# Revit family: L&L_LUCE&LIGHT_SIRI_BLVD_2.0
name_source: partatom
category: Lighting Fixtures
revit_build: Autodesk Revit 2018 (Build: 20181011_1500(x64)
units: mm (PartAtom-declared; Revit-internal decimal feet)

## family parameters
Cut with Voids When Loaded = No
Host = Face
Light Source = Yes
Part Type = Normal
Room Calculation Point = No
Round Connector Dimension = Use Diameter
Shared = No

## types (4) — shared parameters
BIM BADGE = https://bim.archiproducts.com
BODY MATERIAL = DIE-CAST ALUMINIUM ALLOY EN AB 47100
Color Filter = 16777215
Default Elevation = 1219 mm
Description = Urban lighting, projector on arm.
Dimming Lamp Color Temperature Shift = <None>
ENERGY EFFIECIENCY CLASS = A / A+ / A++
Emit Shape Visible in Rendering = Yes
Emit from Rectangle Length = 140 mm  [stored 0.459318 ft]
Emit from Rectangle Width = 120 mm  [stored 0.393701 ft]
HEIGHT = 124 mm  [stored 0.406824 ft]
ILLUMINITECHNICAL PERFORMANCE = 3000K - 38W - 230Vac
LENGTH = 680 mm  [stored 2.23097 ft]
Lamp = LED colour white: 2700K, 3000K, 4000K
Manufacturer = L&L Luce&Light
Model = SIRI BLVD 2.0
POWER CONSUMPTION = 38 W
POWER SUPPLY = 230 Vac
PRODUCT CODE CONFIGURATOR = https://www.lucelight.it
PROTECTION LEVEL = IP 66
SCREEN MATERIAL = EXTRA-CLEAR TEMPERED SERIGRAPHED GLASS
SUPPORT POLE DIAMETER = 60 mm  [stored 0.19685 ft]
TECHNICAL SHEET = https://www.lucelight.it
Tilt Angle = 0.00°
Type Comments = Pole mounting Ø60 mm
URL = https://www.lucelight.it
URL CATALOGUE = https://www.lucelight.it
URL DESCRIPTION = https://www.lucelight.it
URL DXF = https://www.lucelight.it
URL IMAGE = https://www.lucelight.it
WEIGHT KG = 6
WIDTH = 189 mm  [stored 0.620079 ft]

## per-type parameters (varying)
| type | MATERIAL DESCRIPTION | PHOTOMETRIC CURVE | Photometric Web File |
| SIRI BLVD 2.0 A 3000K - Pedestrian zone | Body: die-cast aluminium; Screen: extra-clear tempered and serigraphed glass
Body: die-cast aluminium; Screen: extra-clear tempered and serigraphed glass | SIRI BLVD 2.0 A [3000K 38W 230Vac] | SIRI BLVD 2.0 A [3000K 38W 230Vac].IES |
| SIRI BLVD 2.0 B 3000K - Asymmetrical | Body: die-cast aluminium; Screen: extra-clear tempered and serigraphed glass | SIRI BLVD 2.0 B [3000K 38W 230Vac] | SIRI BLVD 2.0 B [3000K 38W 230Vac].IES |
| SIRI BLVD 2.0 C 3000K - Footpath | Body: die-cast aluminium; Screen: extra-clear tempered and serigraphed glass | SIRI BLVD 2.0 C [3000K 38W 230Vac] | SIRI BLVD 2.0 C [3000K 38W 230Vac].IES |
| SIRI BLVD 2.0 D 3000K - Cyclepath | Body: die-cast aluminium; Screen: extra-clear tempered and serigraphed glass | SIRI BLVD 2.0 D [3000K 38W 230Vac] | SIRI BLVD 2.0 D [3000K 38W 230Vac].IES |

note: [stored X ft] marks values corroborated as IEEE doubles in the binary element streams (Revit-internal decimal feet)
